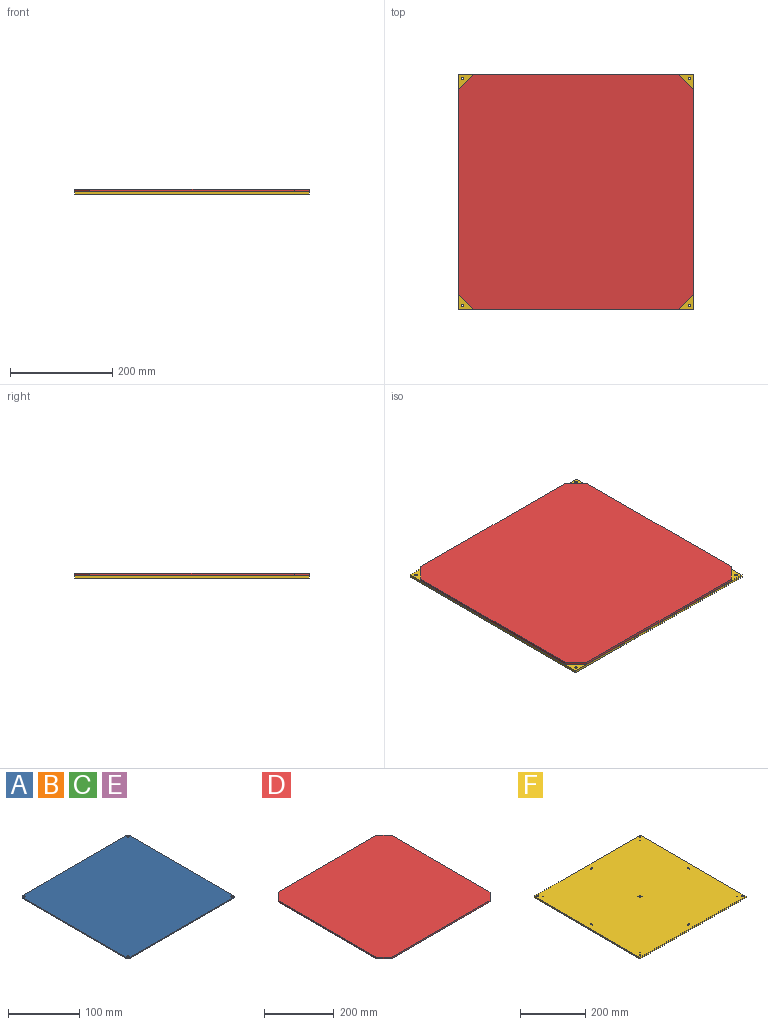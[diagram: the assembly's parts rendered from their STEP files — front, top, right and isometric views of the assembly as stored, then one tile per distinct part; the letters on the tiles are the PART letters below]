
ASSEMBLY  parts=6 mates=5
PART A: 14 faces, bbox 214x214x1.6 mm
  f0: plane 204x1.6mm, normal (0,-1,0), area 326.4mm2, adj f4,f5,f6,f9
  f1: plane 204x1.6mm, normal (1,0,0), area 326.4mm2, adj f4,f5,f6,f7
  f2: plane 204x1.6mm, normal (0,1,0), area 326.4mm2, adj f4,f5,f7,f8
  f3: plane 204x1.6mm, normal (-1,0,0), area 326.4mm2, adj f4,f5,f8,f9
  f4: plane 214x214mm, normal (0,0,1), area 45736.1mm2, adj f0,f1,f2,f3,f6,f7,f8,f9
  f5: plane 214x214mm, normal (0,0,-1), area 45736.1mm2, adj f0,f1,f2,f3,f6,f7,f8,f9
  f6: cylinder r=5mm len=5mm, axis (0,0,1), area 12.6mm2, adj f0,f1,f4,f5
  f7: cylinder r=5mm len=5mm, axis (0,0,-1), area 12.6mm2, adj f1,f2,f4,f5
  f8: cylinder r=5mm len=5mm, axis (0,0,1), area 12.6mm2, adj f2,f3,f4,f5
  f9: cylinder r=5mm len=5mm, axis (0,0,-1), area 12.6mm2, adj f0,f3,f4,f5
  f10: cylinder r=1.75mm len=3.5mm, axis (0,0,-1), area 17.6mm2, adj f4,f5
  f11: cylinder r=1.75mm len=3.5mm, axis (0,0,-1), area 17.6mm2, adj f4,f5
  f12: cylinder r=1.75mm len=3.5mm, axis (0,0,-1), area 17.6mm2, adj f4,f5
  f13: cylinder r=1.75mm len=3.5mm, axis (0,0,-1), area 17.6mm2, adj f4,f5
PART B: same geometry as A
PART C: same geometry as A
PART D: 10 faces, bbox 460x460x5 mm
  f0: plane 400x5mm, normal (0,-1,0), area 2000mm2, adj f4,f5,f6,f9
  f1: plane 400x5mm, normal (1,0,0), area 2000mm2, adj f4,f5,f6,f7
  f2: plane 400x5mm, normal (0,1,0), area 2000mm2, adj f4,f5,f7,f8
  f3: plane 400x5mm, normal (-1,0,0), area 2000mm2, adj f4,f5,f8,f9
  f4: plane 460x460mm, normal (0,0,1), area 209800mm2, adj f0,f1,f2,f3,f6,f7,f8,f9
  f5: plane 460x460mm, normal (0,0,-1), area 209800mm2, adj f0,f1,f2,f3,f6,f7,f8,f9
  f6: plane 30x30mm, normal (0.71,-0.71,0), area 212.1mm2, adj f0,f1,f4,f5
  f7: plane 30x30mm, normal (0.71,0.71,0), area 212.1mm2, adj f1,f2,f4,f5
  f8: plane 30x30mm, normal (-0.71,0.71,0), area 212.1mm2, adj f2,f3,f4,f5
  f9: plane 30x30mm, normal (-0.71,-0.71,0), area 212.1mm2, adj f0,f3,f4,f5
PART E: same geometry as A
PART F: 26 faces, bbox 460x460x5 mm
  f0: plane 460x5mm, normal (0,-1,0), area 2300mm2, adj f1,f3,f4,f5
  f1: plane 460x5mm, normal (1,0,0), area 2300mm2, adj f0,f2,f4,f5
  f2: plane 460x5mm, normal (0,1,0), area 2300mm2, adj f1,f3,f4,f5
  f3: plane 460x5mm, normal (-1,0,0), area 2300mm2, adj f0,f2,f4,f5
  f4: plane 460x460mm, normal (0,0,1), area 211408.4mm2, adj f0,f1,f2,f3,f6,f7,f8,f9
  f5: plane 460x460mm, normal (0,0,-1), area 211408.4mm2, adj f0,f1,f2,f3,f6,f7,f8,f9
  f6: cylinder r=1.5mm len=5mm, axis (0,0,-1), area 47.1mm2, adj f4,f5
  f7: cylinder r=1.5mm len=5mm, axis (0,0,-1), area 47.1mm2, adj f4,f5
  f8: cylinder r=1.5mm len=5mm, axis (0,0,-1), area 47.1mm2, adj f4,f5
  f9: cylinder r=1.5mm len=5mm, axis (0,0,-1), area 47.1mm2, adj f4,f5
  f10: cylinder r=1.5mm len=5mm, axis (0,0,-1), area 47.1mm2, adj f4,f5
  f11: cylinder r=1.5mm len=5mm, axis (0,0,-1), area 47.1mm2, adj f4,f5
  f12: cylinder r=1.5mm len=5mm, axis (0,0,-1), area 47.1mm2, adj f4,f5
  f13: cylinder r=1.5mm len=5mm, axis (0,0,-1), area 47.1mm2, adj f4,f5
  f14: cylinder r=1.5mm len=5mm, axis (0,0,-1), area 47.1mm2, adj f4,f5
  f15: cylinder r=1.5mm len=5mm, axis (0,0,-1), area 47.1mm2, adj f4,f5
  f16: cylinder r=1.5mm len=5mm, axis (0,0,-1), area 47.1mm2, adj f4,f5
  f17: cylinder r=1.5mm len=5mm, axis (0,0,-1), area 47.1mm2, adj f4,f5
  f18: cylinder r=1.5mm len=5mm, axis (0,0,-1), area 47.1mm2, adj f4,f5
  f19: cylinder r=1.5mm len=5mm, axis (0,0,-1), area 47.1mm2, adj f4,f5
  f20: cylinder r=1.5mm len=5mm, axis (0,0,-1), area 47.1mm2, adj f4,f5
  f21: cylinder r=1.5mm len=5mm, axis (0,0,-1), area 47.1mm2, adj f4,f5
  f22: cylinder r=2.5mm len=5mm, axis (0,0,-1), area 78.5mm2, adj f4,f5
  f23: cylinder r=2.5mm len=5mm, axis (0,0,-1), area 78.5mm2, adj f4,f5
  f24: cylinder r=2.5mm len=5mm, axis (0,0,-1), area 78.5mm2, adj f4,f5
  f25: cylinder r=2.5mm len=5mm, axis (0,0,-1), area 78.5mm2, adj f4,f5
PLACE A t=(337.81,-87.72,208.78)mm
PLACE B t=(123.81,-87.72,208.78)mm
PLACE C t=(123.81,126.28,208.78)mm
PLACE D t=(177.84,398.08,215.38)mm
PLACE E t=(337.81,126.28,208.78)mm
PLACE F t=(154.37,916.25,210.38)mm
MATE fastened C.f12 <-> F.f20  axis (0,0,1) through (227.31,22.78,210.38)mm
MATE fastened E.f10 <-> F.f19  axis (0,0,1) through (234.31,22.78,210.38)mm
MATE fastened D.f5 <-> F.f4  axis (0,0,-1) through (230.81,19.28,215.38)mm
MATE fastened A.f13 <-> F.f18  axis (0,0,1) through (234.31,15.78,210.38)mm
MATE fastened B.f11 <-> F.f21  axis (0,0,1) through (227.31,15.78,210.38)mm
